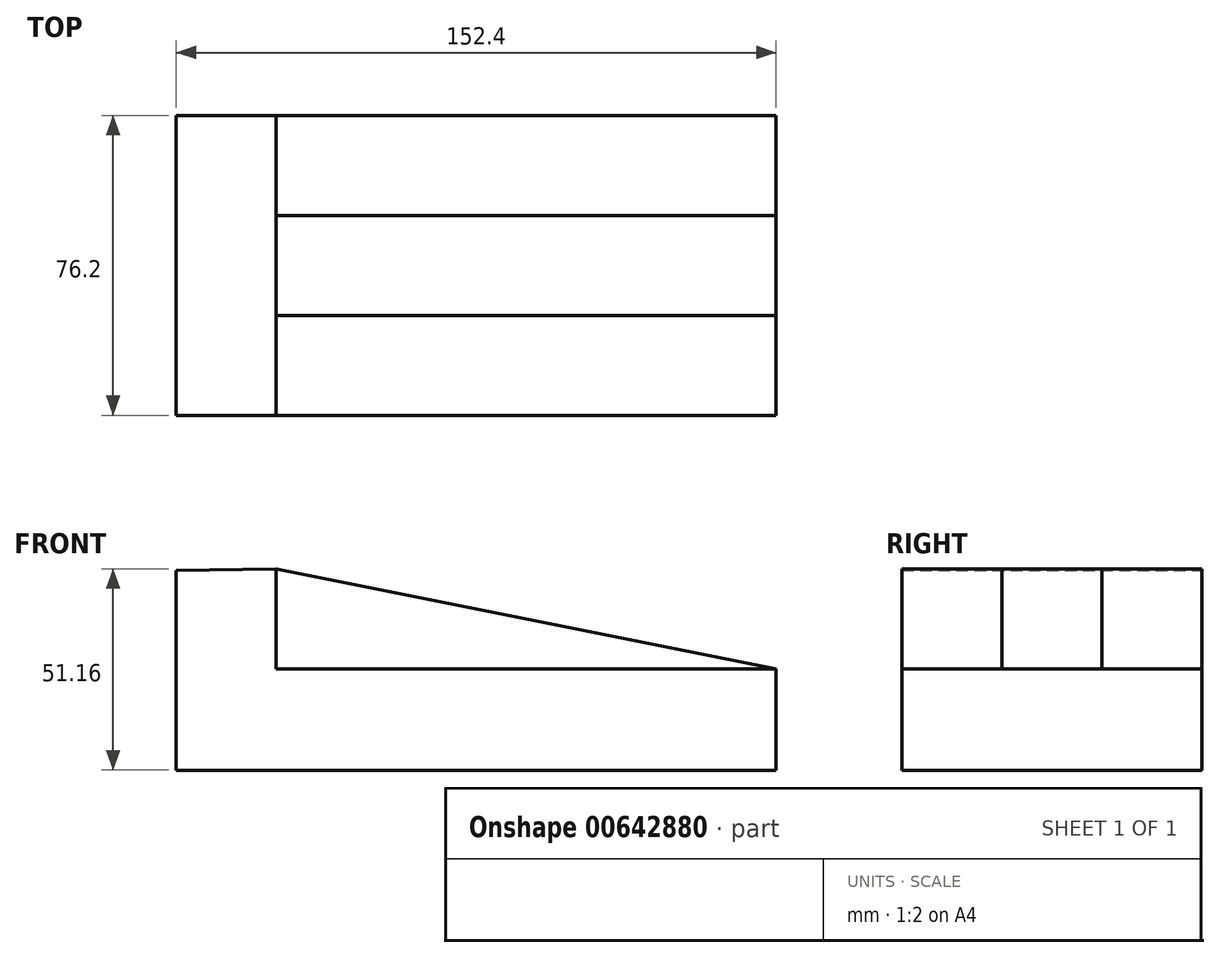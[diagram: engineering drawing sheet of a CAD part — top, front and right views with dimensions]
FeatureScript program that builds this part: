
annotation { "Feature Type Name" : "Feature", "Feature Type Description" : "" }
export const myFeature = defineFeature(function(context is Context, id is Id, definition is map)
    precondition{}
    {
        {
            var Q0;
            Q0=qCreatedBy(makeId("Front.planeOp"),FACE);
            var sketch = newSketch(context, id + "F0", { "sketchPlane" : qUnion([Q0])});
            skLineSegment(sketch, "E0", {"start": v(-125.7, 25.04) * mm, "end": v(-125.7, -25.76) * mm});
            skLineSegment(sketch, "E1", {"start": v(-125.7, -25.76) * mm, "end": v(26.7, -25.76) * mm});
            skLineSegment(sketch, "E2", {"start": v(26.7, -25.76) * mm, "end": v(26.7, 0) * mm});
            skLineSegment(sketch, "E3", {"start": v(26.7, 0) * mm, "end": v(-100.3, 0) * mm});
            skLineSegment(sketch, "E4", {"start": v(-100.3, 0) * mm, "end": v(-100.3, 25.4) * mm});
            skLineSegment(sketch, "E5", {"start": v(-100.3, 25.4) * mm, "end": v(-125.7, 25.04) * mm});
            skSolve(sketch);
        }
        {
            var Q0;
            Q0=makeQuery(id+"F0.imprint","IMPRINT",FACE,{"disambiguationData":[TD([[makeQuery(id+"F0.imprint","IMPRINT",EDGE,{"derivedFrom":sQuery(id+"F0.wireOp",EDGE,"E0")}),1.0]])]});
            extrude(context, id + "F1", {"entities" : qUnion([Q0]), "depth" : 76.2 * mm, "offsetDistance" : 25.4 * mm});
        }
        {
            var Q0;
            Q0=makeQuery(id+"F1.opExtrude","SWEPT_FACE",FACE,{"disambiguationData":[OSD([sQuery(id+"F0.wireOp",EDGE,"E3")])]});
            var sketch = newSketch(context, id + "F2", { "sketchPlane" : qUnion([Q0])});
            skLineSegment(sketch, "E6.top", {"start": v(-100.3, -25.4) * mm, "end": v(26.7, -25.4) * mm});
            skLineSegment(sketch, "E7", {"start": v(-100.3, -25.4) * mm, "end": v(-100.3, -50.8) * mm});
            skLineSegment(sketch, "E8", {"start": v(-100.3, -50.8) * mm, "end": v(26.7, -50.8) * mm});
            skLineSegment(sketch, "E9", {"start": v(26.7, -50.8) * mm, "end": v(26.7, -25.4) * mm});
            skSolve(sketch);
        }
        {
            var Q0;
            Q0=makeQuery(id+"F2.imprint","IMPRINT",FACE,{"disambiguationData":[TD([[makeQuery(id+"F2.imprint","IMPRINT",EDGE,{"derivedFrom":sQuery(id+"F2.wireOp",EDGE,"E6.top")}),-1.0]])]});
            extrude(context, id + "F3", {"entities" : qUnion([Q0]), "operationType" : NewBodyOperationType.ADD, "depth" : 25.4 * mm, "offsetDistance" : 25.4 * mm});
        }
        {
            var Q0;
            Q0=makeQuery(id+"F3.opExtrude","SWEPT_FACE",FACE,{"disambiguationData":[OSD([sQuery(id+"F2.wireOp",EDGE,"E8")])]});
            var sketch = newSketch(context, id + "F4", { "sketchPlane" : qUnion([Q0])});
            skLineSegment(sketch, "E10", {"start": v(-100.3, 25.4) * mm, "end": v(26.7, 0) * mm});
            skSolve(sketch);
        }
        {
            var Q0;
            Q0=makeQuery(id+"F4.imprint","IMPRINT",FACE,{"disambiguationData":[TD([[makeQuery(id+"F4.imprint","IMPRINT",EDGE,{"derivedFrom":sQuery(id+"F4.wireOp",EDGE,"E10")}),1.0]])]});
            extrude(context, id + "F5", {"entities" : qUnion([Q0]), "operationType" : NewBodyOperationType.REMOVE, "oppositeDirection" : true, "depth" : 25.4 * mm, "offsetDistance" : 25.4 * mm});
        }
    });
